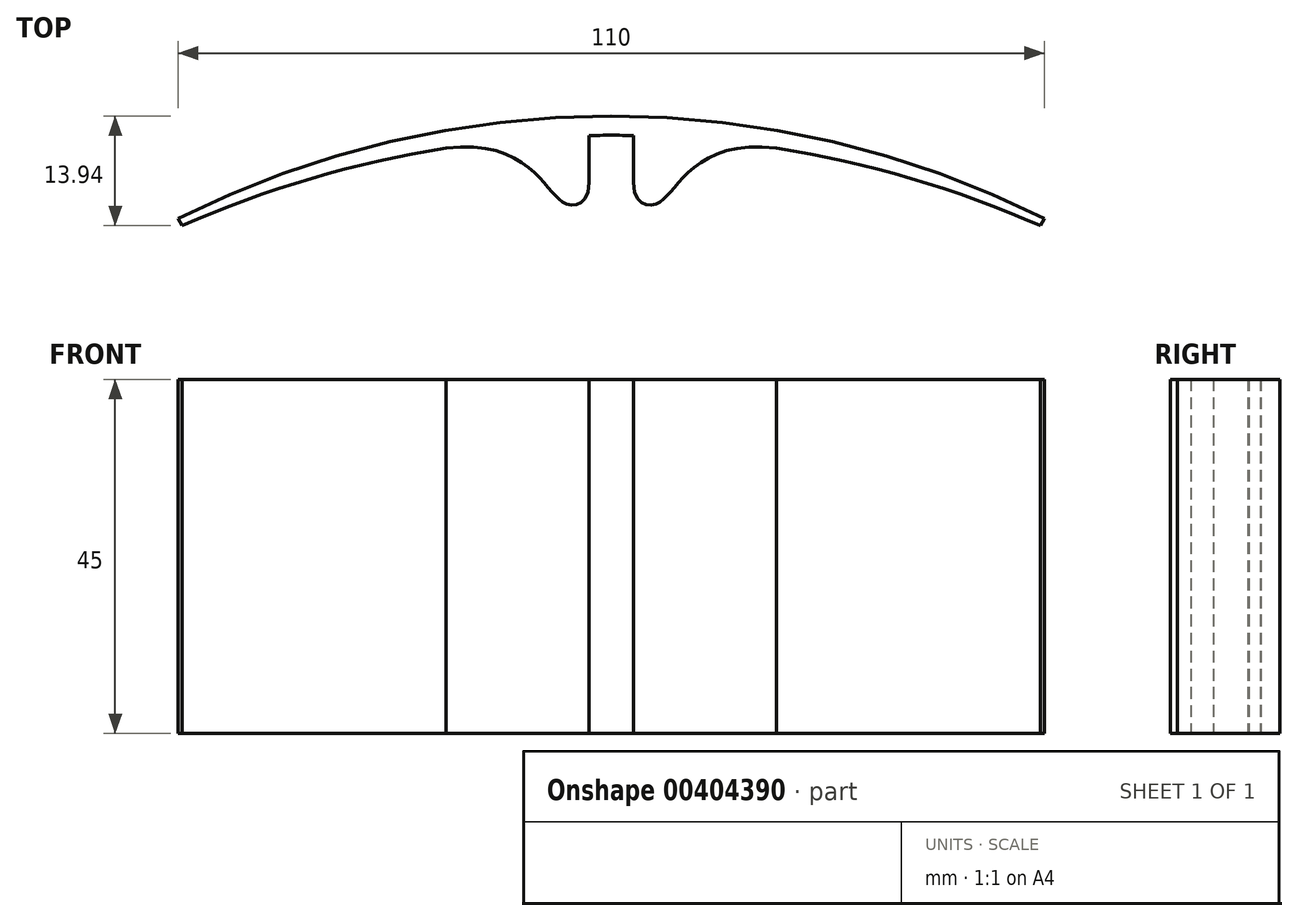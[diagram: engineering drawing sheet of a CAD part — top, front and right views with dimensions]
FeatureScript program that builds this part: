
annotation { "Feature Type Name" : "Feature", "Feature Type Description" : "" }
export const myFeature = defineFeature(function(context is Context, id is Id, definition is map)
    precondition{}
    {
        {
            var Q0;
            Q0=qCreatedBy(makeId("Top.planeOp"),FACE);
            var sketch = newSketch(context, id + "F0", { "sketchPlane" : qUnion([Q0])});
            skArc(sketch, "E0", {"start": v(55, 0) * mm, "mid": v(0, 13) * mm, "end": v(-55, 0) * mm});
            skLineSegment(sketch, "E1", {"start": v(-55, 0) * mm, "end": v(55, 0) * mm, "construction": true});
            skLineSegment(sketch, "E2", {"start": v(-55, 0) * mm, "end": v(-54.53, -0.94) * mm});
            skLineSegment(sketch, "E3", {"start": v(55, 0) * mm, "end": v(54.53, -0.94) * mm});
            skArc(sketch, "E4", {"start": v(54.53, -0.94) * mm, "mid": v(0, 10.55) * mm, "end": v(-54.53, -0.94) * mm});
            skLineSegment(sketch, "E5", {"start": v(0, 10.55) * mm, "end": v(0, 4.55) * mm, "construction": true});
            skPoint(sketch, "E5.endSnap0", {"position": v(0, 10.55) * mm});
            skLineSegment(sketch, "E6", {"start": v(0, 4.55) * mm, "end": v(-2.8, 4.55) * mm, "construction": true});
            skLineSegment(sketch, "E7", {"start": v(-2.8, 4.55) * mm, "end": v(-2.8, 10.52) * mm});
            skFitSpline(sketch, "E8", {"points": [v(-2.8, 4.55) * mm, v(-5.66, 1.85) * mm, v(-8.53, 4.55) * mm, v(-20.97, 8.91) * mm], "startDerivative": vector(-1.54, -32.44) * mm, "endDerivative": vector(-43.88, -5.72) * mm});
            skFitSpline(sketch, "E9.0", {"points": [v(-4.2, 4.62) * mm, v(-4.21, 4.34) * mm, v(-4.27, 3.88) * mm, v(-4.41, 3.44) * mm, v(-4.55, 3.23) * mm, v(-4.63, 3.16) * mm, v(-4.68, 3.13) * mm, v(-4.78, 3.1) * mm, v(-4.93, 3.1) * mm, v(-5.1, 3.13) * mm, v(-5.23, 3.18) * mm, v(-5.35, 3.23) * mm, v(-5.51, 3.32) * mm, v(-5.72, 3.47) * mm, v(-6.03, 3.75) * mm, v(-6.48, 4.27) * mm, v(-7.16, 5.1) * mm, v(-8.02, 6.1) * mm, v(-9.08, 7.14) * mm, v(-10.38, 8.16) * mm, v(-12.46, 9.4) * mm, v(-15.76, 10.5) * mm, v(-19.2, 10.56) * mm, v(-21.15, 10.3) * mm]});
            skLineSegment(sketch, "E9.1", {"start": v(-4.2, 4.58) * mm, "end": v(-4.2, 10.52) * mm});
            skLineSegment(sketch, "E10.MirrorCS", {"start": v(2.8, 4.55) * mm, "end": v(2.8, 10.52) * mm});
            skLineSegment(sketch, "E11.MirrorCS", {"start": v(4.2, 4.58) * mm, "end": v(4.2, 10.52) * mm});
            skFitSpline(sketch, "E12.MirrorCS", {"points": [v(2.8, 4.55) * mm, v(5.66, 1.85) * mm, v(8.53, 4.55) * mm, v(20.97, 8.91) * mm], "startDerivative": vector(1.54, -32.44) * mm, "endDerivative": vector(43.88, -5.72) * mm});
            skFitSpline(sketch, "E13.0", {"points": [v(4.2, 4.62) * mm, v(4.21, 4.34) * mm, v(4.27, 3.88) * mm, v(4.41, 3.44) * mm, v(4.55, 3.23) * mm, v(4.63, 3.16) * mm, v(4.68, 3.13) * mm, v(4.78, 3.1) * mm, v(4.93, 3.1) * mm, v(5.1, 3.13) * mm, v(5.23, 3.18) * mm, v(5.35, 3.23) * mm, v(5.51, 3.32) * mm, v(5.72, 3.47) * mm, v(6.03, 3.75) * mm, v(6.48, 4.27) * mm, v(7.16, 5.1) * mm, v(8.02, 6.1) * mm, v(9.08, 7.14) * mm, v(10.38, 8.16) * mm, v(12.46, 9.4) * mm, v(15.76, 10.5) * mm, v(19.2, 10.56) * mm, v(21.15, 10.3) * mm]});
            skSolve(sketch);
        }
        {
            var Q0;
            {var subQ5=sQuery(id+"F0.wireOp",EDGE,"E10.MirrorCS");Q0=makeQuery(id+"F0.imprint","IMPRINT",FACE,{"disambiguationData":[TD([[makeQuery(id+"F0.imprint","IMPRINT",EDGE,{"derivedFrom":subQ5}),-1.0]])]});}
            var Q1;
            {var subQ0=sQuery(id+"F0.wireOp",EDGE,"E7");Q1=makeQuery(id+"F0.imprint","IMPRINT",FACE,{"disambiguationData":[TD([[makeQuery(id+"F0.imprint","IMPRINT",EDGE,{"derivedFrom":subQ0}),1.0]])]});}
            var Q2;
            Q2=makeQuery(id+"F0.imprint","IMPRINT",FACE,{"disambiguationData":[TD([[makeQuery(id+"F0.imprint","IMPRINT",EDGE,{"derivedFrom":sQuery(id+"F0.wireOp",EDGE,"E0")}),1.0]])]});
            extrude(context, id + "F1", {"entities" : qUnion([Q0, Q1, Q2]), "depth" : 45 * mm});
        }
    });
